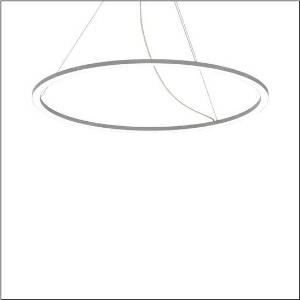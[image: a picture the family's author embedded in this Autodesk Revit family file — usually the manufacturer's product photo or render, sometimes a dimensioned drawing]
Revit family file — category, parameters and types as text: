
# Revit family: silica_r__21_ring-d_5pjbd4d1204a_bd2d
name_source: partatom
category: Lighting Fixtures
units: mm (PartAtom-declared; Revit-internal decimal feet)

## family parameters
Cut with Voids When Loaded = No
Host = Face
Light Source = No
Part Type = Normal
Room Calculation Point = No
Round Connector Dimension = Use Diameter
Shared = No

## types (1)
- Silica® 21 Ring-D (1 x LED, 10840 lm, 125 W, 3000K)
    Apparent Load = 125 VA
    CIE Flux Codes = 37 69 92 100 100
    Color Rendering = 80
    Color Temperature = 3000K
    Default Elevation = 1800 mm
    Description = Silica® 21 Ring-D, suspended luminaire, of PMMA, frosted, light emission: ring underside luminous distribution, primary light characteristic: symmetric, installation type: suspended mounting, LED, rated luminous flux: 10.840lm, luminous efficacy: 87lm/W, light colour: 830, colour temperature: 3000K, control gear: DALI 2, with terminal, 5-pole, mains connection: 230V, AC/DC, 0/50..60Hz, rated input power: 125W, housing, of extruded aluminium section, metallic grey (RAL 9006), diameter: 1.450mm, ceiling canopy, metallic grey (RAL 9006), protection rating (lamp compartment): IP40, insulation class (complete): insulation class I (protective earthing), certification: CE, impact resistance: IK02, permissible operating ambient temperature: 0..+35°C, packaging unit: 1 piece
    Height = 25 mm  [stored 0.082021 ft]
    Lamp = 1 x LED
    Lamp Light Flux = 10840 lm
    Lamp Power = 125 W
    Lamp count = 1
    Length = 1450 mm
    Luminous efficacy = 87 lm/W
    Manufacturer = Siteco
    ModVariant = No
    Model = 5PJBD4D1204A
    Mounting Place = Ceiling
    Mounting Type = Pendant
    Number of Poles = 1
    OnlyDefault = Yes
    Power Factor = 1
    Product Name = Silica® 21 Ring-D
    Product group = suspended luminaire
    ProductGroupID = 905
    Protection Class = Protection class I
    Protection Degree = IP 40
    RLX_Detail_Level = 1
    RLX_Emergency_Light_Flux = 0 lm
    RLX_Emergency_Type = 0
    RLX_Emergency_Type_DB = No
    RlxData = <blob elided: 17949 chars, md5=77019904>
    Socket = socket
    Standby Power = 0 W
    System Light Flux = 10840 lm
    System Power = 125 W
    Type Comments = Product without accessories
    Type Image = l_1251748.jpg
    URL = http://relux.com
    VarID = ---
    Voltage = 0 V
    Weight = 0.00 kg
    Width = 0 mm  [stored 0 ft]

note: [stored X ft] marks values corroborated as IEEE doubles in the binary element streams (Revit-internal decimal feet)

## geometry (parser evidence)
native form markers: Blend x4, Sweep x11
no freeform markers — native parametric forms only
